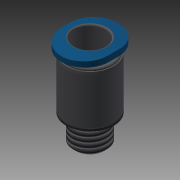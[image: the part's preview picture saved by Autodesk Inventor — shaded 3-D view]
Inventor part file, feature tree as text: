
AUTODESK INVENTOR PART (.ipt)
format: ipt  version: 2018 (Build 220112000, 112)  size: 192,512 bytes
history: native  units: mm
features: other x28, sketch x4, revolve x2, extrude x2, thread x1
ambient origin geometry x8: Origin, YZ Plane, XZ Plane, XY Plane, X Axis, Y Axis, Z Axis, Center Point
bodies: Solid1 (feature_tree)
feature tree (37):
  revolve  "Revolution1"  [1 undecoded]
  thread  "Thread1"  [1 undecoded]
  extrude  "Extrusion1"  TaperAngle=360.0deg  [1 undecoded]
  extrude  "Extrusion2"  TaperAngle=0.0deg  [1 undecoded]
  revolve  "Revolution2"  [1 undecoded]
  other  "ANBAU_XY"
  other  "ANBAU_YZ"
  other  "ANBAU_ZX"
  other  "ANBAU_X"
  other  "ANBAU_Y"
  other  "ANBAU_Z"
  other  "ANBAU_Center"
  other  "ANBAU_STD_XY"
  other  "ANBAU_STD_YZ"
  other  "ANBAU_STD_ZX"
  other  "ANBAU_STD_X"
  other  "ANBAU_STD_Y"
  other  "ANBAU_STD_Z"
  other  "ANBAU_STD_Center"
  other  "CPV_XY"
  other  "CPV_YZ"
  other  "CPV_ZX"
  other  "CPV_X"
  other  "CPV_Y"
  other  "CPV_Z"
  other  "CPV_Center"
  other  "CPV_ANBAU_XY"
  other  "CPV_ANBAU_YZ"
  other  "CPV_ANBAU_ZX"
  other  "CPV_ANBAU_X"
  other  "CPV_ANBAU_Y"
  other  "CPV_ANBAU_Z"
  other  "CPV_ANBAU_Center"
  sketch  "Sketch_1"  dims[d0=360.0deg d1=4.3865mm d2=0.0mm d3=1.5mm d4=0.0mm]
  sketch  "Sketch_2"  dims[d5=7.2mm d6=0.0mm d7=360.0deg]
  sketch  "Sketch_3"  dims[d8=0.0mm d9=0.0mm]
  sketch  "Sketch_4"  dims[d10=0.0mm d11=0.0mm]
note: 5 required parameter values undecoded (feature->parameter linkage not recoverable at this tier; creation-order binding heuristic only, values carry confidence <= 0.55)